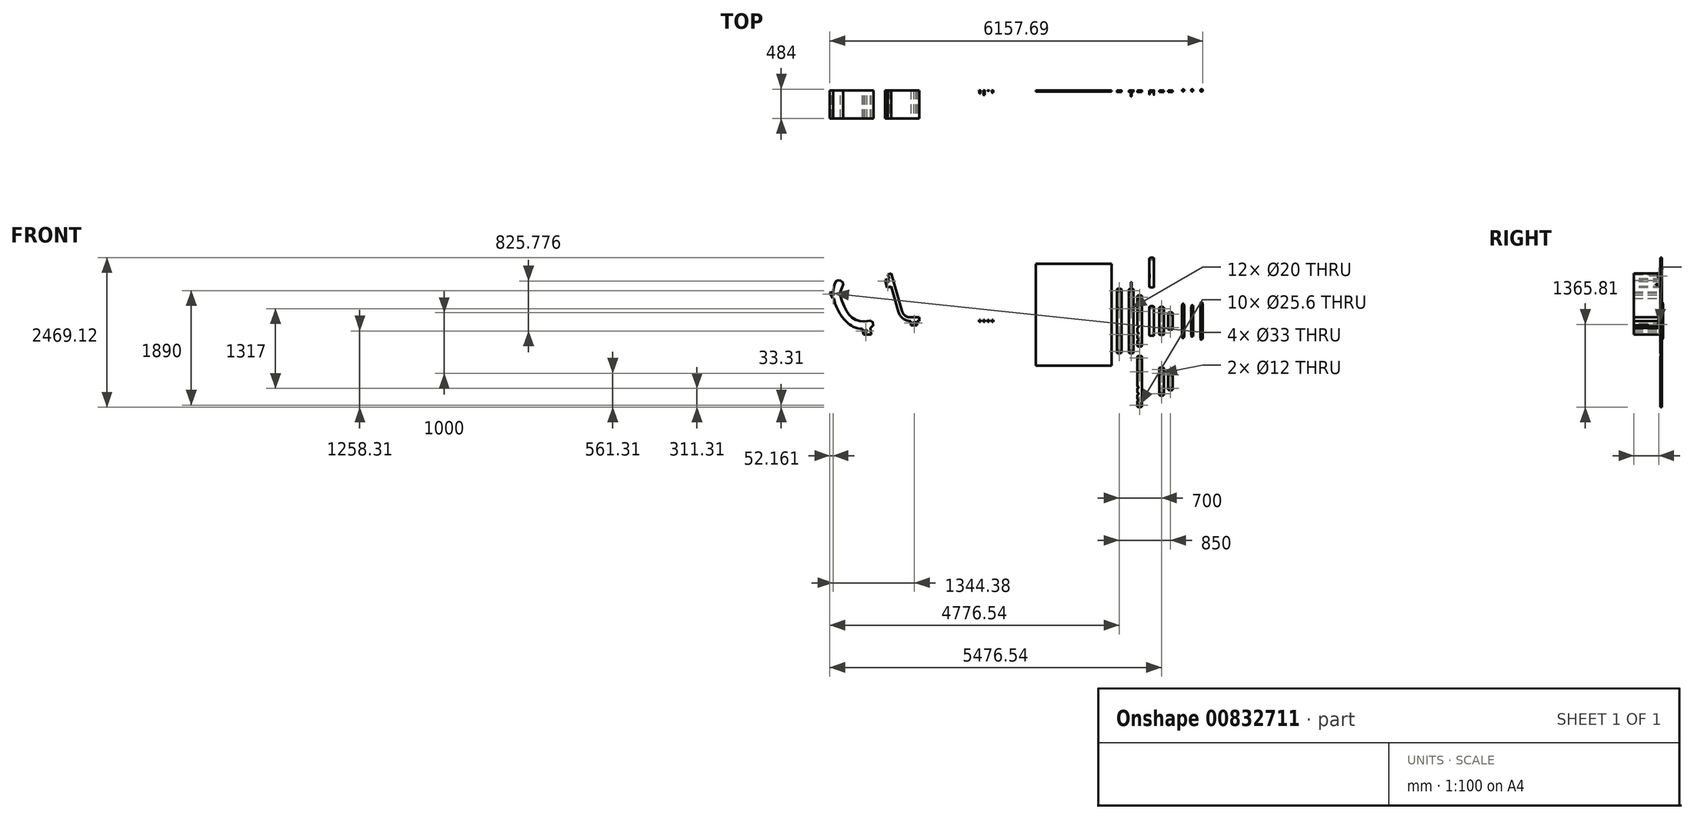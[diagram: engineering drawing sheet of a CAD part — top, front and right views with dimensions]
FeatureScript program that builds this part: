
annotation { "Feature Type Name" : "Feature", "Feature Type Description" : "" }
export const myFeature = defineFeature(function(context is Context, id is Id, definition is map)
    precondition{}
    {
        {
            var Q0;
            Q0=qCreatedBy(makeId("Front.planeOp"),FACE);
            var sketch = newSketch(context, id + "F0", { "sketchPlane" : qUnion([Q0])});
            skLineSegment(sketch, "E0", {"start": v(-38.5, 525.6) * mm, "end": v(-38.5, -525.6) * mm});
            skLineSegment(sketch, "E1", {"start": v(-38.5, -525.6) * mm, "end": v(38.5, -525.6) * mm, "construction": true});
            skLineSegment(sketch, "E2", {"start": v(38.5, -525.6) * mm, "end": v(38.5, 525.6) * mm});
            skLineSegment(sketch, "E3", {"start": v(38.5, 525.6) * mm, "end": v(-38.5, 525.6) * mm, "construction": true});
            skArc(sketch, "E4", {"start": v(38.5, 525.6) * mm, "mid": v(0, 533.3) * mm, "end": v(-38.5, 525.6) * mm});
            skArc(sketch, "E5", {"start": v(-38.5, -525.6) * mm, "mid": v(0, -533.3) * mm, "end": v(38.5, -525.6) * mm});
            skCircle(sketch, "E6", {"center": v(0, 500) * mm, "radius": 12.8 * mm});
            skCircle(sketch, "E7", {"center": v(0, -500) * mm, "radius": 12.8 * mm});
            skPoint(sketch, "E7.centerSnap0", {"position": v(0, 533.3) * mm});
            skCircle(sketch, "E8", {"center": v(0, 205) * mm, "radius": 10 * mm});
            skCircle(sketch, "E9", {"center": v(0, -225) * mm, "radius": 10 * mm});
            skSolve(sketch);
        }
        {
            var Q0;
            Q0 = qSketchRegion(id + "F0", true);
            extrude(context, id + "F1", {"entities" : qUnion([Q0]), "depth" : 25 * mm, "offsetDistance" : 25 * mm});
        }
        {
            var Q0;
            Q0=qCreatedBy(makeId("Front.planeOp"),FACE);
            var sketch = newSketch(context, id + "F2", { "sketchPlane" : qUnion([Q0])});
            skCircle(sketch, "E10", {"center": v(138.5, 390) * mm, "radius": 12.8 * mm});
            skCircle(sketch, "E11", {"center": v(138.5, -390) * mm, "radius": 12.8 * mm});
            skLineSegment(sketch, "E12", {"start": v(100, 415.6) * mm, "end": v(100, -415.6) * mm});
            skLineSegment(sketch, "E13", {"start": v(177, 415.6) * mm, "end": v(177, -415.6) * mm});
            skLineSegment(sketch, "E14", {"start": v(138.5, 390) * mm, "end": v(138.5, -390) * mm, "construction": true});
            skLineSegment(sketch, "E15", {"start": v(100, -415.6) * mm, "end": v(177, -415.6) * mm, "construction": true});
            skLineSegment(sketch, "E16", {"start": v(100, 415.6) * mm, "end": v(177, 415.6) * mm, "construction": true});
            skArc(sketch, "E17", {"start": v(177, 415.6) * mm, "mid": v(138.5, 423.3) * mm, "end": v(100, 415.6) * mm});
            skArc(sketch, "E18", {"start": v(100, -415.6) * mm, "mid": v(138.5, -423.3) * mm, "end": v(177, -415.6) * mm});
            skCircle(sketch, "E19", {"center": v(138.5, 160) * mm, "radius": 10 * mm});
            skCircle(sketch, "E20", {"center": v(138.5, -96) * mm, "radius": 12.8 * mm, "construction": true});
            skSolve(sketch);
        }
        {
            var Q0;
            Q0 = qSketchRegion(id + "F2", true);
            extrude(context, id + "F3", {"entities" : qUnion([Q0]), "depth" : 25 * mm, "offsetDistance" : 25 * mm});
        }
        {
            var Q0;
            Q0=qCreatedBy(makeId("Front.planeOp"),FACE);
            var sketch = newSketch(context, id + "F4", { "sketchPlane" : qUnion([Q0])});
            skLineSegment(sketch, "E21.bottom", {"start": v(300, 238.1) * mm, "end": v(377, 238.1) * mm, "construction": true});
            skLineSegment(sketch, "E21.top", {"start": v(300, -238.1) * mm, "end": v(377, -238.1) * mm, "construction": true});
            skLineSegment(sketch, "E21.left", {"start": v(300, 238.1) * mm, "end": v(300, -238.1) * mm});
            skLineSegment(sketch, "E21.right", {"start": v(377, 238.1) * mm, "end": v(377, -238.1) * mm});
            skArc(sketch, "E22", {"start": v(377, 238.1) * mm, "mid": v(338.5, 245.8) * mm, "end": v(300, 238.1) * mm});
            skArc(sketch, "E23", {"start": v(300, -238.1) * mm, "mid": v(338.5, -245.8) * mm, "end": v(377, -238.1) * mm});
            skLineSegment(sketch, "E24", {"start": v(317.98, 212.5) * mm, "end": v(377, 212.5) * mm, "construction": true});
            skLineSegment(sketch, "E25", {"start": v(309.25, -212.5) * mm, "end": v(377, -212.5) * mm, "construction": true});
            skSolve(sketch);
        }
        {
            var Q0;
            Q0 = qSketchRegion(id + "F4", true);
            extrude(context, id + "F5", {"entities" : qUnion([Q0]), "depth" : 25 * mm, "offsetDistance" : 25 * mm});
        }
        {
            var Q0;
            Q0=makeQuery(id+"F5.opExtrude","SWEPT_FACE",FACE,{"disambiguationData":[OSD([sQuery(id+"F4.wireOp",EDGE,"E21.right")])]});
            var sketch = newSketch(context, id + "F6", { "sketchPlane" : qUnion([Q0])});
            skCircle(sketch, "E26", {"center": v(-12.5, 212.5) * mm, "radius": 6 * mm});
            skSolve(sketch);
        }
        {
            var Q0;
            Q0 = qSketchRegion(id + "F6", true);
            var Q1;
            Q1=makeQuery(id+"F5.opExtrude","SWEPT_FACE",FACE,{"disambiguationData":[OSD([sQuery(id+"F4.wireOp",EDGE,"E21.left")])]});
            extrude(context, id + "F7", {"entities" : qUnion([Q0]), "operationType" : NewBodyOperationType.REMOVE, "endBound" : BoundingType.UP_TO_SURFACE, "oppositeDirection" : true, "depth" : 77 * mm, "endBoundEntityFace" : qUnion([Q1]), "offsetDistance" : 25 * mm});
        }
        {
            var Q0;
            Q0=makeQuery(id+"F1.opExtrude","SWEPT_EDGE",EDGE,{"disambiguationData":[OSD([sQuery(id+"F0.wireOp",EDGE,"E2"),sQuery(id+"F0.wireOp",EDGE,"E4")])]});
            var Q1;
            Q1=makeQuery(id+"F1.opExtrude","SWEPT_EDGE",EDGE,{"disambiguationData":[OSD([sQuery(id+"F0.wireOp",EDGE,"E0"),sQuery(id+"F0.wireOp",EDGE,"E4")])]});
            var Q2;
            Q2=makeQuery(id+"F1.opExtrude","SWEPT_EDGE",EDGE,{"disambiguationData":[OSD([sQuery(id+"F0.wireOp",EDGE,"E2"),sQuery(id+"F0.wireOp",EDGE,"E5")])]});
            var Q3;
            Q3=makeQuery(id+"F1.opExtrude","SWEPT_EDGE",EDGE,{"disambiguationData":[OSD([sQuery(id+"F0.wireOp",EDGE,"E0"),sQuery(id+"F0.wireOp",EDGE,"E5")])]});
            var Q4;
            Q4=makeQuery(id+"F3.opExtrude","SWEPT_EDGE",EDGE,{"disambiguationData":[OSD([sQuery(id+"F2.wireOp",EDGE,"E12"),sQuery(id+"F2.wireOp",EDGE,"E18")])]});
            var Q5;
            Q5=makeQuery(id+"F3.opExtrude","SWEPT_EDGE",EDGE,{"disambiguationData":[OSD([sQuery(id+"F2.wireOp",EDGE,"E13"),sQuery(id+"F2.wireOp",EDGE,"E18")])]});
            var Q6;
            Q6=makeQuery(id+"F3.opExtrude","SWEPT_EDGE",EDGE,{"disambiguationData":[OSD([sQuery(id+"F2.wireOp",EDGE,"E12"),sQuery(id+"F2.wireOp",EDGE,"E17")])]});
            var Q7;
            Q7=makeQuery(id+"F3.opExtrude","SWEPT_EDGE",EDGE,{"disambiguationData":[OSD([sQuery(id+"F2.wireOp",EDGE,"E13"),sQuery(id+"F2.wireOp",EDGE,"E17")])]});
            var Q8;
            Q8=makeQuery(id+"F5.opExtrude","SWEPT_EDGE",EDGE,{"disambiguationData":[OSD([sQuery(id+"F4.wireOp",EDGE,"E21.right"),sQuery(id+"F4.wireOp",EDGE,"E23")])]});
            var Q9;
            Q9=makeQuery(id+"F5.opExtrude","SWEPT_EDGE",EDGE,{"disambiguationData":[OSD([sQuery(id+"F4.wireOp",EDGE,"E21.left"),sQuery(id+"F4.wireOp",EDGE,"E23")])]});
            var Q10;
            Q10=makeQuery(id+"F5.opExtrude","SWEPT_EDGE",EDGE,{"disambiguationData":[OSD([sQuery(id+"F4.wireOp",EDGE,"E21.right"),sQuery(id+"F4.wireOp",EDGE,"E22")])]});
            var Q11;
            Q11=makeQuery(id+"F5.opExtrude","SWEPT_EDGE",EDGE,{"disambiguationData":[OSD([sQuery(id+"F4.wireOp",EDGE,"E21.left"),sQuery(id+"F4.wireOp",EDGE,"E22")])]});
            fillet(context, id + "F8", {"entities" : qUnion([Q0, Q1, Q2, Q3, Q4, Q5, Q6, Q7, Q8, Q9, Q10, Q11]), "radius" : 10 * mm, "tangentPropagation" : true, "allowEdgeOverflow" : false});
        }
        {
            var Q0;
            Q0=qCreatedBy(makeId("Front.planeOp"),FACE);
            var sketch = newSketch(context, id + "F9", { "sketchPlane" : qUnion([Q0])});
            skLineSegment(sketch, "E27.bottom", {"start": v(461.5, 225.6) * mm, "end": v(538.5, 225.6) * mm, "construction": true});
            skLineSegment(sketch, "E27.top", {"start": v(461.5, -225.6) * mm, "end": v(538.5, -225.6) * mm, "construction": true});
            skLineSegment(sketch, "E27.left", {"start": v(461.5, 225.6) * mm, "end": v(461.5, -225.6) * mm});
            skLineSegment(sketch, "E27.right", {"start": v(538.5, 225.6) * mm, "end": v(538.5, -225.6) * mm});
            skCircle(sketch, "E28", {"center": v(500, 200) * mm, "radius": 10 * mm});
            skCircle(sketch, "E29", {"center": v(500, -200) * mm, "radius": 12.8 * mm});
            skLineSegment(sketch, "E30", {"start": v(500, 200) * mm, "end": v(500, -200) * mm, "construction": true});
            skArc(sketch, "E31", {"start": v(461.5, -225.6) * mm, "mid": v(500, -233.3) * mm, "end": v(538.5, -225.6) * mm});
            skArc(sketch, "E32", {"start": v(538.5, 225.6) * mm, "mid": v(500, 233.3) * mm, "end": v(461.5, 225.6) * mm});
            skCircle(sketch, "E33", {"center": v(500, 138) * mm, "radius": 6 * mm});
            skSolve(sketch);
        }
        {
            var Q0;
            Q0 = qSketchRegion(id + "F9", true);
            extrude(context, id + "F10", {"entities" : qUnion([Q0]), "depth" : 25 * mm, "offsetDistance" : 25 * mm});
        }
        {
            var Q0;
            Q0=qCreatedBy(makeId("Front.planeOp"),FACE);
            var sketch = newSketch(context, id + "F11", { "sketchPlane" : qUnion([Q0])});
            skLineSegment(sketch, "E34.bottom", {"start": v(611.5, 135.6) * mm, "end": v(688.5, 135.6) * mm, "construction": true});
            skLineSegment(sketch, "E34.top", {"start": v(611.5, -137.6) * mm, "end": v(688.5, -137.6) * mm, "construction": true});
            skLineSegment(sketch, "E34.left", {"start": v(611.5, 135.6) * mm, "end": v(611.5, -137.6) * mm});
            skLineSegment(sketch, "E34.right", {"start": v(688.5, 135.6) * mm, "end": v(688.5, -137.6) * mm});
            skCircle(sketch, "E35", {"center": v(650, 110) * mm, "radius": 10 * mm});
            skCircle(sketch, "E36", {"center": v(650, -112) * mm, "radius": 10 * mm});
            skLineSegment(sketch, "E37", {"start": v(650, 110) * mm, "end": v(650, -112) * mm, "construction": true});
            skArc(sketch, "E38", {"start": v(688.5, 135.6) * mm, "mid": v(650, 143.3) * mm, "end": v(611.5, 135.6) * mm});
            skArc(sketch, "E39", {"start": v(611.5, -137.6) * mm, "mid": v(650, -145.3) * mm, "end": v(688.5, -137.6) * mm});
            skLineSegment(sketch, "E40", {"start": v(591.68, 162.5) * mm, "end": v(739.94, 162.5) * mm, "construction": true});
            skSolve(sketch);
        }
        {
            var Q0;
            Q0 = qSketchRegion(id + "F11", true);
            extrude(context, id + "F12", {"entities" : qUnion([Q0]), "depth" : 25 * mm, "offsetDistance" : 25 * mm});
        }
        {
            var Q0;
            Q0=qCreatedBy(makeId("Front.planeOp"),FACE);
            var sketch = newSketch(context, id + "F13", { "sketchPlane" : qUnion([Q0])});
            skLineSegment(sketch, "E41.bottom", {"start": v(-1573.72, 942.98) * mm, "end": v(-325.98, 942.98) * mm});
            skLineSegment(sketch, "E41.top", {"start": v(-1573.72, -735.53) * mm, "end": v(-325.98, -735.53) * mm});
            skLineSegment(sketch, "E41.left", {"start": v(-1573.72, 942.98) * mm, "end": v(-1573.72, -735.53) * mm});
            skLineSegment(sketch, "E41.right", {"start": v(-325.98, 942.98) * mm, "end": v(-325.98, -735.53) * mm});
            skSolve(sketch);
        }
        {
            var Q0;
            Q0 = qSketchRegion(id + "F13", true);
            extrude(context, id + "F14", {"entities" : qUnion([Q0]), "depth" : 20 * mm, "offsetDistance" : 25 * mm});
        }
        {
            var Q0;
            Q0=qCreatedBy(makeId("Top.planeOp"),FACE);
            var sketch = newSketch(context, id + "F15", { "sketchPlane" : qUnion([Q0])});
            skCircle(sketch, "E42", {"center": v(857.86, 0) * mm, "radius": 17.5 * mm});
            skSolve(sketch);
        }
        {
            var Q0;
            Q0 = qSketchRegion(id + "F15", true);
            extrude(context, id + "F16", {"entities" : qUnion([Q0]), "depth" : 257 * mm, "offsetDistance" : 25 * mm, "hasSecondDirection" : true, "secondDirectionOppositeDirection" : true, "secondDirectionDepth" : 257 * mm});
        }
        {
            var Q0;
            Q0=qCreatedBy(makeId("Top.planeOp"),FACE);
            var sketch = newSketch(context, id + "F17", { "sketchPlane" : qUnion([Q0])});
            skCircle(sketch, "E43", {"center": v(1007, 0) * mm, "radius": 17.5 * mm});
            skSolve(sketch);
        }
        {
            var Q0;
            Q0 = qSketchRegion(id + "F17", true);
            extrude(context, id + "F18", {"entities" : qUnion([Q0]), "depth" : 232 * mm, "offsetDistance" : 25 * mm, "hasSecondDirection" : true, "secondDirectionOppositeDirection" : true, "secondDirectionDepth" : 232 * mm});
        }
        {
            var Q0;
            Q0=qCreatedBy(makeId("Top.planeOp"),FACE);
            var sketch = newSketch(context, id + "F19", { "sketchPlane" : qUnion([Q0])});
            skCircle(sketch, "E44", {"center": v(1161.15, 0) * mm, "radius": 20 * mm});
            skSolve(sketch);
        }
        {
            var Q0;
            Q0 = qSketchRegion(id + "F19", true);
            extrude(context, id + "F20", {"entities" : qUnion([Q0]), "depth" : 282 * mm, "offsetDistance" : 25 * mm, "hasSecondDirection" : true, "secondDirectionOppositeDirection" : true, "secondDirectionDepth" : 282 * mm});
        }
        {
            var Q0;
            Q0=makeQuery(id+"F3.opExtrude","CAP_FACE",FACE,{"disambiguationData":[OSD([sQuery(id+"F2.wireOp",EDGE,"E10"),sQuery(id+"F2.wireOp",EDGE,"E11"),sQuery(id+"F2.wireOp",EDGE,"E12"),sQuery(id+"F2.wireOp",EDGE,"E13"),sQuery(id+"F2.wireOp",EDGE,"E17"),sQuery(id+"F2.wireOp",EDGE,"E18"),sQuery(id+"F2.wireOp",EDGE,"E19")])],"isStart":false});
            var sketch = newSketch(context, id + "F21", { "sketchPlane" : qUnion([Q0])});
            skCircle(sketch, "E45", {"center": v(100, -96) * mm, "radius": 20 * mm});
            skLineSegment(sketch, "E46", {"start": v(138.5, 160) * mm, "end": v(59.14, 160) * mm, "construction": true});
            skSolve(sketch);
        }
        {
            var Q0;
            Q0 = qSketchRegion(id + "F21", true);
            extrude(context, id + "F22", {"entities" : qUnion([Q0]), "operationType" : NewBodyOperationType.REMOVE, "oppositeDirection" : true, "depth" : 25 * mm, "offsetDistance" : 25 * mm});
        }
        {
            var Q0;
            Q0=makeQuery(id+"F5.opExtrude","SWEPT_FACE",FACE,{"disambiguationData":[OSD([sQuery(id+"F4.wireOp",EDGE,"E21.right")])]});
            var sketch = newSketch(context, id + "F23", { "sketchPlane" : qUnion([Q0])});
            skLineSegment(sketch, "E47", {"start": v(-28, -27.5) * mm, "end": v(-28, -87.5) * mm});
            skLineSegment(sketch, "E48", {"start": v(-28, -87.5) * mm, "end": v(-59.23, -76.33) * mm});
            skLineSegment(sketch, "E49", {"start": v(-28, -27.5) * mm, "end": v(-59.23, -38.67) * mm});
            skArc(sketch, "E50", {"start": v(-59.23, -38.67) * mm, "mid": v(-72.5, -57.5) * mm, "end": v(-59.23, -76.33) * mm});
            skCircle(sketch, "E51", {"center": v(-52.5, -57.5) * mm, "radius": 10 * mm});
            skLineSegment(sketch, "E52", {"start": v(-52.5, -57.5) * mm, "end": v(29.16, -57.5) * mm, "construction": true});
            skCircle(sketch, "E53.0", {"center": v(-12.5, 212.5) * mm, "radius": 6 * mm, "construction": true});
            skSolve(sketch);
        }
        {
            var Q0;
            Q0=makeQuery(id+"F5.opExtrude","CAP_FACE",FACE,{"disambiguationData":[OSD([sQuery(id+"F4.wireOp",EDGE,"E21.left"),sQuery(id+"F4.wireOp",EDGE,"E21.right"),sQuery(id+"F4.wireOp",EDGE,"E22"),sQuery(id+"F4.wireOp",EDGE,"E23")])],"isStart":false});
            var sketch = newSketch(context, id + "F24", { "sketchPlane" : qUnion([Q0])});
            skLineSegment(sketch, "E54.bottom", {"start": v(372, -27.5) * mm, "end": v(377, -27.5) * mm});
            skLineSegment(sketch, "E54.top", {"start": v(372, -87.5) * mm, "end": v(377, -87.5) * mm});
            skLineSegment(sketch, "E54.left", {"start": v(372, -27.5) * mm, "end": v(372, -87.5) * mm});
            skLineSegment(sketch, "E54.right", {"start": v(377, -27.5) * mm, "end": v(377, -87.5) * mm});
            skSolve(sketch);
        }
        {
            var Q0;
            Q0=makeQuery(id+"F5.opExtrude","SWEPT_BODY",BODY,{"disambiguationData":[OSD([sQuery(id+"F4.wireOp",EDGE,"E21.left"),sQuery(id+"F4.wireOp",EDGE,"E21.right"),sQuery(id+"F4.wireOp",EDGE,"E22"),sQuery(id+"F4.wireOp",EDGE,"E23")])]});
            transform(context, id + "F25", {"entities" : qUnion([Q0]), "transformType" : TransformType.TRANSLATION_3D, "dx" : 0 * mm, "dy" : 0 * mm, "dz" : 800 * mm, "makeCopy" : true});
        }
        {
            var Q0;
            Q0=makeQuery(id+"F24.imprint","IMPRINT",FACE,{"disambiguationData":[TD([[makeQuery(id+"F24.imprint","IMPRINT",EDGE,{"derivedFrom":sQuery(id+"F24.wireOp",EDGE,"E54.bottom")}),-1.0]])]});
            extrude(context, id + "F26", {"entities" : qUnion([Q0]), "operationType" : NewBodyOperationType.ADD, "depth" : 3 * mm, "offsetDistance" : 25 * mm});
        }
        {
            var Q0;
            Q0=makeQuery(id+"F3.opExtrude","CAP_FACE",FACE,{"disambiguationData":[OSD([sQuery(id+"F2.wireOp",EDGE,"E10"),sQuery(id+"F2.wireOp",EDGE,"E11"),sQuery(id+"F2.wireOp",EDGE,"E12"),sQuery(id+"F2.wireOp",EDGE,"E13"),sQuery(id+"F2.wireOp",EDGE,"E17"),sQuery(id+"F2.wireOp",EDGE,"E18"),sQuery(id+"F2.wireOp",EDGE,"E19")])],"isStart":false});
            var sketch = newSketch(context, id + "F27", { "sketchPlane" : qUnion([Q0])});
            skCircle(sketch, "E55", {"center": v(100, -306) * mm, "radius": 20 * mm});
            skArc(sketch, "E56.0", {"start": v(100, -116) * mm, "mid": v(120, -96) * mm, "end": v(100, -76) * mm, "construction": true});
            skCircle(sketch, "E57", {"center": v(100, -201) * mm, "radius": 20 * mm});
            skSolve(sketch);
        }
        {
            var Q0;
            Q0 = qSketchRegion(id + "F27", true);
            extrude(context, id + "F28", {"entities" : qUnion([Q0]), "operationType" : NewBodyOperationType.REMOVE, "oppositeDirection" : true, "depth" : 25 * mm, "offsetDistance" : 25 * mm});
        }
        {
            var Q0;
            Q0 = qSketchRegion(id + "F23", true);
            extrude(context, id + "F29", {"entities" : qUnion([Q0]), "operationType" : NewBodyOperationType.ADD, "oppositeDirection" : true, "depth" : 5 * mm, "offsetDistance" : 25 * mm});
        }
        {
            var Q0;
            Q0=makeQuery(id+"F22.boolean.opBoolean","COPY",FACE,{"derivedFrom":makeQuery(id+"F22.opExtrude","SWEPT_FACE",FACE,{"disambiguationData":[OSD([sQuery(id+"F21.wireOp",EDGE,"E45")])]})});
            var Q1;
            Q1=makeQuery(id+"F28.boolean.opBoolean","COPY",FACE,{"derivedFrom":makeQuery(id+"F28.opExtrude","SWEPT_FACE",FACE,{"disambiguationData":[OSD([sQuery(id+"F27.wireOp",EDGE,"E57")])]})});
            var Q2;
            Q2=makeQuery(id+"F28.boolean.opBoolean","COPY",FACE,{"derivedFrom":makeQuery(id+"F28.opExtrude","SWEPT_FACE",FACE,{"disambiguationData":[OSD([sQuery(id+"F27.wireOp",EDGE,"E55")])]})});
            fillet(context, id + "F30", {"entities" : qUnion([Q0, Q1, Q2]), "radius" : 2 * mm, "tangentPropagation" : true, "allowEdgeOverflow" : false});
        }
        {
            var Q0;
            Q0=qCreatedBy(makeId("Front.planeOp"),FACE);
            var sketch = newSketch(context, id + "F31", { "sketchPlane" : qUnion([Q0])});
            skLineSegment(sketch, "E58", {"start": v(-3800, 0) * mm, "end": v(-3500, 0) * mm});
            skLineSegment(sketch, "E59", {"start": v(-3500, 0) * mm, "end": v(-3500, 60) * mm});
            skLineSegment(sketch, "E60", {"start": v(-3500, 60) * mm, "end": v(-3754.65, 60) * mm});
            skLineSegment(sketch, "E61", {"start": v(-3754.65, 60) * mm, "end": v(-3960.53, 786.02) * mm});
            skLineSegment(sketch, "E62", {"start": v(-3960.53, 786.02) * mm, "end": v(-4018.26, 769.65) * mm});
            skLineSegment(sketch, "E63", {"start": v(-4018.26, 769.65) * mm, "end": v(-3800, 0) * mm});
            skSolve(sketch);
        }
        {
            var Q0;
            Q0 = qSketchRegion(id + "F31", true);
            extrude(context, id + "F32", {"entities" : qUnion([Q0]), "depth" : 464 * mm, "offsetDistance" : 25 * mm});
        }
        {
            var Q0;
            Q0=makeQuery(id+"F1.opExtrude","SWEPT_BODY",BODY,{"disambiguationData":[OSD([sQuery(id+"F0.wireOp",EDGE,"E0"),sQuery(id+"F0.wireOp",EDGE,"E2"),sQuery(id+"F0.wireOp",EDGE,"E4"),sQuery(id+"F0.wireOp",EDGE,"E5"),sQuery(id+"F0.wireOp",EDGE,"E6"),sQuery(id+"F0.wireOp",EDGE,"E7"),sQuery(id+"F0.wireOp",EDGE,"E8"),sQuery(id+"F0.wireOp",EDGE,"E9")])]});
            transform(context, id + "F33", {"entities" : qUnion([Q0]), "transformType" : TransformType.TRANSLATION_3D, "dx" : -200 * mm, "dy" : 0 * mm, "dz" : 0 * mm, "makeCopy" : true});
        }
        {
            var Q0;
            Q0=makeQuery(id+"F3.opExtrude","SWEPT_BODY",BODY,{"disambiguationData":[OSD([sQuery(id+"F2.wireOp",EDGE,"E10"),sQuery(id+"F2.wireOp",EDGE,"E11"),sQuery(id+"F2.wireOp",EDGE,"E12"),sQuery(id+"F2.wireOp",EDGE,"E13"),sQuery(id+"F2.wireOp",EDGE,"E17"),sQuery(id+"F2.wireOp",EDGE,"E18"),sQuery(id+"F2.wireOp",EDGE,"E19")])]});
            transform(context, id + "F34", {"entities" : qUnion([Q0]), "transformType" : TransformType.TRANSLATION_3D, "dx" : 0 * mm, "dy" : 0 * mm, "dz" : -1000 * mm, "makeCopy" : true});
        }
        {
            var Q0;
            Q0=makeQuery(id+"F10.opExtrude","SWEPT_BODY",BODY,{"disambiguationData":[OSD([sQuery(id+"F9.wireOp",EDGE,"E27.left"),sQuery(id+"F9.wireOp",EDGE,"E27.right"),sQuery(id+"F9.wireOp",EDGE,"E28"),sQuery(id+"F9.wireOp",EDGE,"E29"),sQuery(id+"F9.wireOp",EDGE,"E31"),sQuery(id+"F9.wireOp",EDGE,"E32"),sQuery(id+"F9.wireOp",EDGE,"E33")])]});
            transform(context, id + "F35", {"entities" : qUnion([Q0]), "transformType" : TransformType.TRANSLATION_3D, "dx" : 0 * mm, "dy" : 0 * mm, "dz" : -1000 * mm, "makeCopy" : true});
        }
        {
            var Q0;
            Q0=makeQuery(id+"F12.opExtrude","SWEPT_BODY",BODY,{"disambiguationData":[OSD([sQuery(id+"F11.wireOp",EDGE,"E34.left"),sQuery(id+"F11.wireOp",EDGE,"E34.right"),sQuery(id+"F11.wireOp",EDGE,"E35"),sQuery(id+"F11.wireOp",EDGE,"E36"),sQuery(id+"F11.wireOp",EDGE,"E38"),sQuery(id+"F11.wireOp",EDGE,"E39")])]});
            transform(context, id + "F36", {"entities" : qUnion([Q0]), "transformType" : TransformType.TRANSLATION_3D, "dx" : 0 * mm, "dy" : 0 * mm, "dz" : -1000 * mm, "makeCopy" : true});
        }
        {
            var Q0;
            Q0=makeQuery(id+"F32.opExtrude","SWEPT_EDGE",EDGE,{"disambiguationData":[OSD([sQuery(id+"F31.wireOp",EDGE,"E58"),sQuery(id+"F31.wireOp",EDGE,"E63")])]});
            fillet(context, id + "F37", {"entities" : qUnion([Q0]), "radius" : 200 * mm, "tangentPropagation" : true, "allowEdgeOverflow" : false});
        }
        {
            var Q0;
            Q0=makeQuery(id+"F32.opExtrude","SWEPT_EDGE",EDGE,{"disambiguationData":[OSD([sQuery(id+"F31.wireOp",EDGE,"E60"),sQuery(id+"F31.wireOp",EDGE,"E61")])]});
            fillet(context, id + "F38", {"entities" : qUnion([Q0]), "radius" : 140 * mm, "tangentPropagation" : true, "allowEdgeOverflow" : false});
        }
        {
            var Q0;
            Q0=makeQuery(id+"F32.opExtrude","CAP_FACE",FACE,{"disambiguationData":[OSD([sQuery(id+"F31.wireOp",EDGE,"E58"),sQuery(id+"F31.wireOp",EDGE,"E59"),sQuery(id+"F31.wireOp",EDGE,"E60"),sQuery(id+"F31.wireOp",EDGE,"E61"),sQuery(id+"F31.wireOp",EDGE,"E62"),sQuery(id+"F31.wireOp",EDGE,"E63")])],"isStart":false});
            var sketch = newSketch(context, id + "F39", { "sketchPlane" : qUnion([Q0])});
            skPoint(sketch, "E64", {"position": v(-4018.56, 660.78) * mm});
            skPoint(sketch, "E65", {"position": v(-3580, -30) * mm});
            skLineSegment(sketch, "E66", {"start": v(-4018.56, 660.78) * mm, "end": v(-3931.98, 685.33) * mm, "construction": true});
            skLineSegment(sketch, "E67", {"start": v(-3580, -30) * mm, "end": v(-3580, 60) * mm, "construction": true});
            skCircle(sketch, "E68", {"center": v(-4018.56, 660.78) * mm, "radius": 16.5 * mm});
            skCircle(sketch, "E69", {"center": v(-3580, -30) * mm, "radius": 16.5 * mm});
            skLineSegment(sketch, "E70", {"start": v(-3997.89, 697.82) * mm, "end": v(-4065.23, 678.73) * mm});
            skLineSegment(sketch, "E71", {"start": v(-4065.23, 678.73) * mm, "end": v(-4029.77, 553.66) * mm});
            skLineSegment(sketch, "E72", {"start": v(-4029.77, 553.66) * mm, "end": v(-3962.42, 572.75) * mm});
            skLineSegment(sketch, "E73.bottom", {"start": v(-3540, 0) * mm, "end": v(-3640, 0) * mm});
            skLineSegment(sketch, "E73.top", {"start": v(-3540, -70) * mm, "end": v(-3640, -70) * mm});
            skLineSegment(sketch, "E73.left", {"start": v(-3540, 0) * mm, "end": v(-3540, -70) * mm});
            skLineSegment(sketch, "E73.right", {"start": v(-3640, 0) * mm, "end": v(-3640, -70) * mm});
            skSolve(sketch);
        }
        {
            var Q0;
            Q0=makeQuery(id+"F39.imprint","IMPRINT",FACE,{"disambiguationData":[TD([[makeQuery(id+"F39.imprint","IMPRINT",EDGE,{"derivedFrom":sQuery(id+"F39.wireOp",EDGE,"E69")}),-1.0]])]});
            var Q1;
            Q1=makeQuery(id+"F39.imprint","IMPRINT",FACE,{"disambiguationData":[TD([[makeQuery(id+"F39.imprint","IMPRINT",EDGE,{"derivedFrom":sQuery(id+"F39.wireOp",EDGE,"E68")}),-1.0]])]});
            var Q2;
            Q2=makeQuery(id+"F32.opExtrude","CAP_FACE",FACE,{"disambiguationData":[OSD([sQuery(id+"F31.wireOp",EDGE,"E58"),sQuery(id+"F31.wireOp",EDGE,"E59"),sQuery(id+"F31.wireOp",EDGE,"E60"),sQuery(id+"F31.wireOp",EDGE,"E61"),sQuery(id+"F31.wireOp",EDGE,"E62"),sQuery(id+"F31.wireOp",EDGE,"E63")])],"isStart":true});
            extrude(context, id + "F40", {"entities" : qUnion([Q0, Q1]), "operationType" : NewBodyOperationType.ADD, "endBound" : BoundingType.UP_TO_SURFACE, "oppositeDirection" : true, "depth" : 25 * mm, "endBoundEntityFace" : qUnion([Q2]), "offsetDistance" : 25 * mm});
        }
        {
            var Q0;
            Q0=makeQuery(id+"F16.opExtrude","CAP_FACE",FACE,{"disambiguationData":[OSD([sQuery(id+"F15.wireOp",EDGE,"E42")])],"isStart":false});
            var sketch = newSketch(context, id + "F41", { "sketchPlane" : qUnion([Q0])});
            skCircle(sketch, "E74", {"center": v(857.86, 0) * mm, "radius": 12.8 * mm});
            skSolve(sketch);
        }
        {
            var Q0;
            Q0 = qSketchRegion(id + "F41", true);
            extrude(context, id + "F42", {"entities" : qUnion([Q0]), "operationType" : NewBodyOperationType.ADD, "depth" : 25 * mm, "offsetDistance" : 25 * mm});
        }
        {
            var Q0;
            Q0=makeQuery(id+"F16.opExtrude","CAP_FACE",FACE,{"disambiguationData":[OSD([sQuery(id+"F15.wireOp",EDGE,"E42")])],"isStart":true});
            var sketch = newSketch(context, id + "F43", { "sketchPlane" : qUnion([Q0])});
            skCircle(sketch, "E75", {"center": v(857.86, 0) * mm, "radius": 12.8 * mm});
            skSolve(sketch);
        }
        {
            var Q0;
            Q0 = qSketchRegion(id + "F43", true);
            extrude(context, id + "F44", {"entities" : qUnion([Q0]), "operationType" : NewBodyOperationType.ADD, "depth" : 25 * mm, "offsetDistance" : 25 * mm});
        }
        {
            var Q0;
            Q0=makeQuery(id+"F18.opExtrude","CAP_FACE",FACE,{"disambiguationData":[OSD([sQuery(id+"F17.wireOp",EDGE,"E43")])],"isStart":true});
            var sketch = newSketch(context, id + "F45", { "sketchPlane" : qUnion([Q0])});
            skCircle(sketch, "E76", {"center": v(1007, 0) * mm, "radius": 12.8 * mm});
            skSolve(sketch);
        }
        {
            var Q0;
            Q0 = qSketchRegion(id + "F45", true);
            extrude(context, id + "F46", {"entities" : qUnion([Q0]), "operationType" : NewBodyOperationType.ADD, "depth" : 25 * mm, "offsetDistance" : 25 * mm});
        }
        {
            var Q0;
            Q0=makeQuery(id+"F18.opExtrude","CAP_FACE",FACE,{"disambiguationData":[OSD([sQuery(id+"F17.wireOp",EDGE,"E43")])],"isStart":false});
            var sketch = newSketch(context, id + "F47", { "sketchPlane" : qUnion([Q0])});
            skCircle(sketch, "E77", {"center": v(1007, 0) * mm, "radius": 12.8 * mm});
            skSolve(sketch);
        }
        {
            var Q0;
            Q0 = qSketchRegion(id + "F47", true);
            extrude(context, id + "F48", {"entities" : qUnion([Q0]), "operationType" : NewBodyOperationType.ADD, "depth" : 25 * mm, "offsetDistance" : 25 * mm});
        }
        {
            var Q0;
            Q0=makeQuery(id+"F20.opExtrude","CAP_FACE",FACE,{"disambiguationData":[OSD([sQuery(id+"F19.wireOp",EDGE,"E44")])],"isStart":true});
            var sketch = newSketch(context, id + "F49", { "sketchPlane" : qUnion([Q0])});
            skCircle(sketch, "E78", {"center": v(1161.15, 0) * mm, "radius": 12.8 * mm});
            skSolve(sketch);
        }
        {
            var Q0;
            Q0 = qSketchRegion(id + "F49", true);
            extrude(context, id + "F50", {"entities" : qUnion([Q0]), "operationType" : NewBodyOperationType.ADD, "depth" : 25 * mm, "offsetDistance" : 25 * mm});
        }
        {
            var Q0;
            Q0=makeQuery(id+"F20.opExtrude","CAP_FACE",FACE,{"disambiguationData":[OSD([sQuery(id+"F19.wireOp",EDGE,"E44")])],"isStart":false});
            var sketch = newSketch(context, id + "F51", { "sketchPlane" : qUnion([Q0])});
            skCircle(sketch, "E79", {"center": v(1161.15, 0) * mm, "radius": 12.8 * mm});
            skSolve(sketch);
        }
        {
            var Q0;
            Q0 = qSketchRegion(id + "F51", true);
            extrude(context, id + "F52", {"entities" : qUnion([Q0]), "operationType" : NewBodyOperationType.ADD, "depth" : 25 * mm, "offsetDistance" : 25 * mm});
        }
        {
            var Q0;
            Q0=qCreatedBy(makeId("Front.planeOp"),FACE);
            var sketch = newSketch(context, id + "F53", { "sketchPlane" : qUnion([Q0])});
            skCircle(sketch, "E80", {"center": v(-2500, 0) * mm, "radius": 15 * mm, "construction": true});
            skLineSegment(sketch, "E81.0", {"start": v(-2508.66, 15) * mm, "end": v(-2491.34, 15) * mm});
            skLineSegment(sketch, "E81.1", {"start": v(-2491.34, 15) * mm, "end": v(-2482.68, 0) * mm});
            skLineSegment(sketch, "E81.2", {"start": v(-2482.68, 0) * mm, "end": v(-2491.34, -15) * mm});
            skLineSegment(sketch, "E81.3", {"start": v(-2491.34, -15) * mm, "end": v(-2508.66, -15) * mm});
            skLineSegment(sketch, "E81.4", {"start": v(-2508.66, -15) * mm, "end": v(-2517.32, 0) * mm});
            skLineSegment(sketch, "E81.5", {"start": v(-2517.32, 0) * mm, "end": v(-2508.66, 15) * mm});
            skPoint(sketch, "E81.0.midPoint", {"position": v(-2500, 15) * mm});
            skCircle(sketch, "E82", {"center": v(-2500, 0) * mm, "radius": 21 * mm, "construction": true});
            skCircle(sketch, "E83.cCircle", {"center": v(-2430, 0) * mm, "radius": 15 * mm, "construction": true});
            skLineSegment(sketch, "E83.0", {"start": v(-2438.66, 15) * mm, "end": v(-2421.34, 15) * mm});
            skLineSegment(sketch, "E83.1", {"start": v(-2421.34, 15) * mm, "end": v(-2412.68, 0) * mm});
            skLineSegment(sketch, "E83.2", {"start": v(-2412.68, 0) * mm, "end": v(-2421.34, -15) * mm});
            skLineSegment(sketch, "E83.3", {"start": v(-2421.34, -15) * mm, "end": v(-2438.66, -15) * mm});
            skLineSegment(sketch, "E83.4", {"start": v(-2438.66, -15) * mm, "end": v(-2447.32, 0) * mm});
            skLineSegment(sketch, "E83.5", {"start": v(-2447.32, 0) * mm, "end": v(-2438.66, 15) * mm});
            skPoint(sketch, "E83.0.midPoint", {"position": v(-2430, 15) * mm});
            skCircle(sketch, "E84.cCircle", {"center": v(-2360, 0) * mm, "radius": 15 * mm, "construction": true});
            skLineSegment(sketch, "E84.0", {"start": v(-2368.66, 15) * mm, "end": v(-2351.34, 15) * mm});
            skLineSegment(sketch, "E84.1", {"start": v(-2351.34, 15) * mm, "end": v(-2342.68, 0) * mm});
            skLineSegment(sketch, "E84.2", {"start": v(-2342.68, 0) * mm, "end": v(-2351.34, -15) * mm});
            skLineSegment(sketch, "E84.3", {"start": v(-2351.34, -15) * mm, "end": v(-2368.66, -15) * mm});
            skLineSegment(sketch, "E84.4", {"start": v(-2368.66, -15) * mm, "end": v(-2377.32, 0) * mm});
            skLineSegment(sketch, "E84.5", {"start": v(-2377.32, 0) * mm, "end": v(-2368.66, 15) * mm});
            skPoint(sketch, "E84.0.midPoint", {"position": v(-2360, 15) * mm});
            skCircle(sketch, "E85", {"center": v(-2360, 0) * mm, "radius": 10 * mm});
            skCircle(sketch, "E86.cCircle", {"center": v(-2290, 0) * mm, "radius": 15 * mm, "construction": true});
            skLineSegment(sketch, "E86.0", {"start": v(-2298.66, 15) * mm, "end": v(-2281.34, 15) * mm});
            skLineSegment(sketch, "E86.1", {"start": v(-2281.34, 15) * mm, "end": v(-2272.68, 0) * mm});
            skLineSegment(sketch, "E86.2", {"start": v(-2272.68, 0) * mm, "end": v(-2281.34, -15) * mm});
            skLineSegment(sketch, "E86.3", {"start": v(-2281.34, -15) * mm, "end": v(-2298.66, -15) * mm});
            skLineSegment(sketch, "E86.4", {"start": v(-2298.66, -15) * mm, "end": v(-2307.32, 0) * mm});
            skLineSegment(sketch, "E86.5", {"start": v(-2307.32, 0) * mm, "end": v(-2298.66, 15) * mm});
            skPoint(sketch, "E86.0.midPoint", {"position": v(-2290, 15) * mm});
            skSolve(sketch);
        }
        {
            var Q0;
            Q0 = qSketchRegion(id + "F53", true);
            extrude(context, id + "F54", {"entities" : qUnion([Q0]), "depth" : 8 * mm, "offsetDistance" : 25 * mm});
        }
        {
            var Q0;
            Q0=makeQuery(id+"F54.opExtrude","CAP_FACE",FACE,{"disambiguationData":[OSD([sQuery(id+"F53.wireOp",EDGE,"E81.0"),sQuery(id+"F53.wireOp",EDGE,"E81.1"),sQuery(id+"F53.wireOp",EDGE,"E81.2"),sQuery(id+"F53.wireOp",EDGE,"E81.3"),sQuery(id+"F53.wireOp",EDGE,"E81.4"),sQuery(id+"F53.wireOp",EDGE,"E81.5")])],"isStart":false});
            var sketch = newSketch(context, id + "F55", { "sketchPlane" : qUnion([Q0])});
            skCircle(sketch, "E87", {"center": v(-2500, 0) * mm, "radius": 10 * mm});
            skPoint(sketch, "E87.centerSnap0", {"position": v(-2500, 15) * mm});
            skSolve(sketch);
        }
        {
            var Q0;
            Q0 = qSketchRegion(id + "F55", true);
            extrude(context, id + "F56", {"entities" : qUnion([Q0]), "operationType" : NewBodyOperationType.ADD, "depth" : 42 * mm, "offsetDistance" : 25 * mm});
        }
        {
            var Q0;
            Q0=makeQuery(id+"F54.opExtrude","CAP_FACE",FACE,{"disambiguationData":[OSD([sQuery(id+"F53.wireOp",EDGE,"E83.0"),sQuery(id+"F53.wireOp",EDGE,"E83.1"),sQuery(id+"F53.wireOp",EDGE,"E83.2"),sQuery(id+"F53.wireOp",EDGE,"E83.3"),sQuery(id+"F53.wireOp",EDGE,"E83.4"),sQuery(id+"F53.wireOp",EDGE,"E83.5")])],"isStart":false});
            var sketch = newSketch(context, id + "F57", { "sketchPlane" : qUnion([Q0])});
            skCircle(sketch, "E88", {"center": v(-2430, 0) * mm, "radius": 10 * mm});
            skSolve(sketch);
        }
        {
            var Q0;
            Q0 = qSketchRegion(id + "F57", true);
            extrude(context, id + "F58", {"entities" : qUnion([Q0]), "operationType" : NewBodyOperationType.ADD, "depth" : 67 * mm, "offsetDistance" : 25 * mm});
        }
        {
            var Q0;
            Q0=makeQuery(id+"F54.opExtrude","CAP_FACE",FACE,{"disambiguationData":[OSD([sQuery(id+"F53.wireOp",EDGE,"E86.0"),sQuery(id+"F53.wireOp",EDGE,"E86.1"),sQuery(id+"F53.wireOp",EDGE,"E86.2"),sQuery(id+"F53.wireOp",EDGE,"E86.3"),sQuery(id+"F53.wireOp",EDGE,"E86.4"),sQuery(id+"F53.wireOp",EDGE,"E86.5")])],"isStart":false});
            var sketch = newSketch(context, id + "F59", { "sketchPlane" : qUnion([Q0])});
            skCircle(sketch, "E89", {"center": v(-2290, 0) * mm, "radius": 10 * mm});
            skSolve(sketch);
        }
        {
            var Q0;
            Q0 = qSketchRegion(id + "F59", true);
            extrude(context, id + "F60", {"entities" : qUnion([Q0]), "operationType" : NewBodyOperationType.ADD, "depth" : 30 * mm, "offsetDistance" : 25 * mm});
        }
        {
            var Q0;
            Q0=makeQuery(id+"F10.opExtrude","CAP_FACE",FACE,{"disambiguationData":[OSD([sQuery(id+"F9.wireOp",EDGE,"E27.left"),sQuery(id+"F9.wireOp",EDGE,"E27.right"),sQuery(id+"F9.wireOp",EDGE,"E28"),sQuery(id+"F9.wireOp",EDGE,"E29"),sQuery(id+"F9.wireOp",EDGE,"E31"),sQuery(id+"F9.wireOp",EDGE,"E32"),sQuery(id+"F9.wireOp",EDGE,"E33")])],"isStart":false});
            var sketch = newSketch(context, id + "F61", { "sketchPlane" : qUnion([Q0])});
            skCircle(sketch, "E90", {"center": v(500, 138) * mm, "radius": 10 * mm});
            skSolve(sketch);
        }
        {
            var Q0;
            Q0 = qSketchRegion(id + "F61", true);
            extrude(context, id + "F62", {"entities" : qUnion([Q0]), "operationType" : NewBodyOperationType.REMOVE, "depth" : 8 * mm, "offsetDistance" : 25 * mm});
        }
        {
            var Q0;
            Q0=makeQuery(id+"F25.opPattern","COPY",FACE,{"derivedFrom":makeQuery(id+"F5.opExtrude","SWEPT_FACE",FACE,{"disambiguationData":[OSD([sQuery(id+"F4.wireOp",EDGE,"E21.right")])]}),"instanceName":"1"});
            var sketch = newSketch(context, id + "F63", { "sketchPlane" : qUnion([Q0])});
            skCircle(sketch, "E91", {"center": v(-12.5, 1012.5) * mm, "radius": 10 * mm});
            skSolve(sketch);
        }
        {
            var Q0;
            Q0=qCreatedBy(makeId("Front.planeOp"),FACE);
            var sketch = newSketch(context, id + "F64", { "sketchPlane" : qUnion([Q0])});
            skCircle(sketch, "E92.cCircle", {"center": v(0, 600) * mm, "radius": 8 * mm, "construction": true});
            skLineSegment(sketch, "E92.0", {"start": v(-4.62, 608) * mm, "end": v(4.62, 608) * mm});
            skLineSegment(sketch, "E92.1", {"start": v(4.62, 608) * mm, "end": v(9.24, 600) * mm});
            skLineSegment(sketch, "E92.2", {"start": v(9.24, 600) * mm, "end": v(4.62, 592) * mm});
            skLineSegment(sketch, "E92.3", {"start": v(4.62, 592) * mm, "end": v(-4.62, 592) * mm});
            skLineSegment(sketch, "E92.4", {"start": v(-4.62, 592) * mm, "end": v(-9.24, 600) * mm});
            skLineSegment(sketch, "E92.5", {"start": v(-9.24, 600) * mm, "end": v(-4.62, 608) * mm});
            skPoint(sketch, "E92.0.midPoint", {"position": v(0, 608) * mm});
            skCircle(sketch, "E93", {"center": v(0, 600) * mm, "radius": 10 * mm, "construction": true});
            skCircle(sketch, "E94.cCircle", {"center": v(0, 630) * mm, "radius": 8 * mm, "construction": true});
            skLineSegment(sketch, "E94.0", {"start": v(-4.62, 638) * mm, "end": v(4.62, 638) * mm});
            skLineSegment(sketch, "E94.1", {"start": v(4.62, 638) * mm, "end": v(9.24, 630) * mm});
            skLineSegment(sketch, "E94.2", {"start": v(9.24, 630) * mm, "end": v(4.62, 622) * mm});
            skLineSegment(sketch, "E94.3", {"start": v(4.62, 622) * mm, "end": v(-4.62, 622) * mm});
            skLineSegment(sketch, "E94.4", {"start": v(-4.62, 622) * mm, "end": v(-9.24, 630) * mm});
            skLineSegment(sketch, "E94.5", {"start": v(-9.24, 630) * mm, "end": v(-4.62, 638) * mm});
            skPoint(sketch, "E94.0.midPoint", {"position": v(0, 638) * mm});
            skCircle(sketch, "E95", {"center": v(0, 630) * mm, "radius": 6 * mm});
            skSolve(sketch);
        }
        {
            var Q0;
            Q0=makeQuery(id+"F64.imprint","IMPRINT",FACE,{"disambiguationData":[TD([[makeQuery(id+"F64.imprint","IMPRINT",EDGE,{"derivedFrom":sQuery(id+"F64.wireOp",EDGE,"E92.0")}),-1.0]])]});
            var Q1;
            Q1=makeQuery(id+"F64.imprint","IMPRINT",FACE,{"disambiguationData":[TD([[makeQuery(id+"F64.imprint","IMPRINT",EDGE,{"derivedFrom":sQuery(id+"F64.wireOp",EDGE,"E94.0")}),-1.0]])]});
            var Q2;
            Q2=sQuery(id+"F64.wireOp",EDGE,"E93");
            extrude(context, id + "F65", {"entities" : qUnion([Q0, Q1]), "surfaceEntities" : qUnion([Q2]), "depth" : 5 * mm, "offsetDistance" : 25 * mm});
        }
        {
            var Q0;
            Q0=makeQuery(id+"F65.opExtrude","CAP_FACE",FACE,{"disambiguationData":[OSD([sQuery(id+"F64.wireOp",EDGE,"E92.0"),sQuery(id+"F64.wireOp",EDGE,"E92.1"),sQuery(id+"F64.wireOp",EDGE,"E92.2"),sQuery(id+"F64.wireOp",EDGE,"E92.3"),sQuery(id+"F64.wireOp",EDGE,"E92.4"),sQuery(id+"F64.wireOp",EDGE,"E92.5")])],"isStart":false});
            var sketch = newSketch(context, id + "F66", { "sketchPlane" : qUnion([Q0])});
            skCircle(sketch, "E96", {"center": v(0, 600) * mm, "radius": 6 * mm});
            skSolve(sketch);
        }
        {
            var Q0;
            Q0 = qSketchRegion(id + "F66", true);
            extrude(context, id + "F67", {"entities" : qUnion([Q0]), "operationType" : NewBodyOperationType.ADD, "depth" : 97 * mm, "offsetDistance" : 25 * mm});
        }
        {
            var Q0;
            Q0=qCreatedBy(makeId("Front.planeOp"),FACE);
            var sketch = newSketch(context, id + "F68", { "sketchPlane" : qUnion([Q0])});
            skCircle(sketch, "E97.cCircle", {"center": v(0, 570) * mm, "radius": 7 * mm, "construction": true});
            skLineSegment(sketch, "E97.0", {"start": v(-4.04, 577) * mm, "end": v(4.04, 577) * mm});
            skLineSegment(sketch, "E97.1", {"start": v(4.04, 577) * mm, "end": v(8.08, 570) * mm});
            skLineSegment(sketch, "E97.2", {"start": v(8.08, 570) * mm, "end": v(4.04, 563) * mm});
            skLineSegment(sketch, "E97.3", {"start": v(4.04, 563) * mm, "end": v(-4.04, 563) * mm});
            skLineSegment(sketch, "E97.4", {"start": v(-4.04, 563) * mm, "end": v(-8.08, 570) * mm});
            skLineSegment(sketch, "E97.5", {"start": v(-8.08, 570) * mm, "end": v(-4.04, 577) * mm});
            skPoint(sketch, "E97.0.midPoint", {"position": v(0, 577) * mm});
            skSolve(sketch);
        }
        {
            var Q0;
            Q0 = qSketchRegion(id + "F68", true);
            extrude(context, id + "F69", {"entities" : qUnion([Q0]), "depth" : 3 * mm, "offsetDistance" : 25 * mm});
        }
        {
            var Q0;
            Q0=makeQuery(id+"F69.opExtrude","CAP_FACE",FACE,{"disambiguationData":[OSD([sQuery(id+"F68.wireOp",EDGE,"E97.0"),sQuery(id+"F68.wireOp",EDGE,"E97.1"),sQuery(id+"F68.wireOp",EDGE,"E97.2"),sQuery(id+"F68.wireOp",EDGE,"E97.3"),sQuery(id+"F68.wireOp",EDGE,"E97.4"),sQuery(id+"F68.wireOp",EDGE,"E97.5")])],"isStart":false});
            var sketch = newSketch(context, id + "F70", { "sketchPlane" : qUnion([Q0])});
            skCircle(sketch, "E98", {"center": v(0, 570) * mm, "radius": 4 * mm});
            skSolve(sketch);
        }
        {
            var Q0;
            Q0 = qSketchRegion(id + "F70", true);
            extrude(context, id + "F71", {"entities" : qUnion([Q0]), "operationType" : NewBodyOperationType.ADD, "depth" : 13 * mm, "offsetDistance" : 25 * mm});
        }
        {
            var Q0;
            Q0=qCreatedBy(makeId("Front.planeOp"),FACE);
            var sketch = newSketch(context, id + "F72", { "sketchPlane" : qUnion([Q0])});
            skCircle(sketch, "E99", {"center": v(-4924.38, 445.87) * mm, "radius": 16.5 * mm});
            skCircle(sketch, "E100", {"center": v(-4380, -165) * mm, "radius": 16.5 * mm});
            skCircle(sketch, "E101.0", {"center": v(-3580, -30) * mm, "radius": 16.5 * mm, "construction": true});
            skCircle(sketch, "E102.0", {"center": v(-4018.56, 660.78) * mm, "radius": 16.5 * mm, "construction": true});
            skFitSpline(sketch, "E103", {"points": [v(-4285.55, 0) * mm, v(-4263.83, -82.96) * mm, v(-4527.36, -117.42) * mm, v(-4751.42, 41.89) * mm, v(-4862.59, 223.1) * mm, v(-4920.48, 440.9) * mm, v(-4897.1, 605.72) * mm, v(-4861.84, 667.96) * mm, v(-4817.48, 672.43) * mm, v(-4768.38, 645.04) * mm, v(-4760.24, 587.33) * mm, v(-4803.14, 468.85) * mm, v(-4733.68, 225.77) * mm, v(-4627.46, 70.51) * mm, v(-4480.38, 0) * mm, v(-4357.62, 0) * mm, v(-4285.55, 0) * mm]});
            skLineSegment(sketch, "E104", {"start": v(-4920.34, 482.88) * mm, "end": v(-4976.54, 468.15) * mm});
            skLineSegment(sketch, "E105", {"start": v(-4976.54, 468.15) * mm, "end": v(-4929.96, 375.69) * mm});
            skLineSegment(sketch, "E106", {"start": v(-4929.96, 375.69) * mm, "end": v(-4912.28, 375.69) * mm});
            skLineSegment(sketch, "E107", {"start": v(-4439.67, -130.69) * mm, "end": v(-4418.5, -221.82) * mm});
            skLineSegment(sketch, "E108", {"start": v(-4418.5, -221.82) * mm, "end": v(-4294.26, -221.82) * mm});
            skLineSegment(sketch, "E109", {"start": v(-4294.26, -221.82) * mm, "end": v(-4308.25, -114.89) * mm});
            skSolve(sketch);
        }
        {
            var Q0;
            Q0 = qSketchRegion(id + "F72", true);
            var Q1;
            {var subQ0=sQuery(id+"F31.wireOp",EDGE,"E63");Q1=makeQuery(id+"F40.boolean.opBoolean","MERGE",FACE,{"derivedFrom":[makeQuery(id+"F32.opExtrude","CAP_FACE",FACE,{"disambiguationData":[OSD([sQuery(id+"F31.wireOp",EDGE,"E58"),sQuery(id+"F31.wireOp",EDGE,"E59"),sQuery(id+"F31.wireOp",EDGE,"E60"),sQuery(id+"F31.wireOp",EDGE,"E61"),sQuery(id+"F31.wireOp",EDGE,"E62"),subQ0])],"isStart":false}),makeQuery(id+"F40.opExtrude","CAP_FACE",FACE,{"disambiguationData":[OSD([subQ0,sQuery(id+"F39.wireOp",EDGE,"E68"),sQuery(id+"F39.wireOp",EDGE,"E70"),sQuery(id+"F39.wireOp",EDGE,"E71"),sQuery(id+"F39.wireOp",EDGE,"E72")])],"isStart":true}),makeQuery(id+"F40.opExtrude","CAP_FACE",FACE,{"disambiguationData":[OSD([sQuery(id+"F39.wireOp",EDGE,"E69"),sQuery(id+"F39.wireOp",EDGE,"E73.bottom"),sQuery(id+"F39.wireOp",EDGE,"E73.top"),sQuery(id+"F39.wireOp",EDGE,"E73.left"),sQuery(id+"F39.wireOp",EDGE,"E73.right")])],"isStart":true})]});}
            extrude(context, id + "F73", {"entities" : qUnion([Q0]), "endBound" : BoundingType.UP_TO_SURFACE, "depth" : 25 * mm, "endBoundEntityFace" : qUnion([Q1]), "offsetDistance" : 25 * mm});
        }
        {
            var Q0;
            Q0=makeQuery(id+"F25.opPattern","COPY",FACE,{"derivedFrom":makeQuery(id+"F5.opExtrude","SWEPT_FACE",FACE,{"disambiguationData":[OSD([sQuery(id+"F4.wireOp",EDGE,"E21.left")])]}),"instanceName":"1"});
            var sketch = newSketch(context, id + "F74", { "sketchPlane" : qUnion([Q0])});
            skLineSegment(sketch, "E110", {"start": v(28, 772.5) * mm, "end": v(59.23, 761.33) * mm});
            skLineSegment(sketch, "E111", {"start": v(28, 712.5) * mm, "end": v(59.23, 723.67) * mm});
            skArc(sketch, "E112", {"start": v(59.23, 723.67) * mm, "mid": v(72.5, 742.5) * mm, "end": v(59.23, 761.33) * mm});
            skLineSegment(sketch, "E113", {"start": v(28, 772.5) * mm, "end": v(25, 772.5) * mm});
            skLineSegment(sketch, "E114", {"start": v(28, 712.5) * mm, "end": v(25, 712.5) * mm});
            skLineSegment(sketch, "E115", {"start": v(25, 712.5) * mm, "end": v(25, 772.5) * mm});
            skCircle(sketch, "E116", {"center": v(52.5, 742.5) * mm, "radius": 10 * mm});
            skSolve(sketch);
        }
        {
            var Q0;
            Q0 = qSketchRegion(id + "F74", true);
            extrude(context, id + "F75", {"entities" : qUnion([Q0]), "operationType" : NewBodyOperationType.ADD, "oppositeDirection" : true, "depth" : 5 * mm, "offsetDistance" : 25 * mm});
        }
    });
